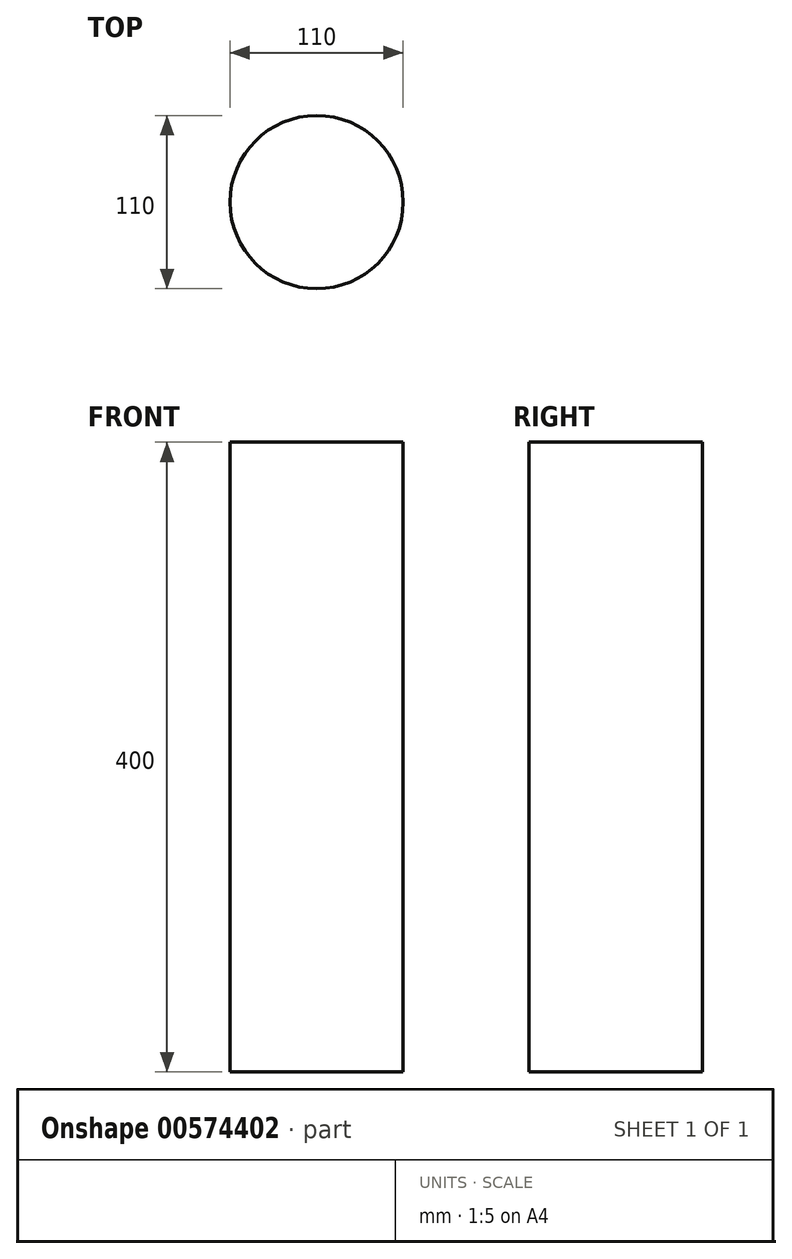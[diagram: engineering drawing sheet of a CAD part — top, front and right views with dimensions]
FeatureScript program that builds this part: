
annotation { "Feature Type Name" : "Feature", "Feature Type Description" : "" }
export const myFeature = defineFeature(function(context is Context, id is Id, definition is map)
    precondition{}
    {
        {
            var Q0;
            Q0=qCreatedBy(makeId("Top.planeOp"),FACE);
            var sketch = newSketch(context, id + "F0", { "sketchPlane" : qUnion([Q0])});
            skCircle(sketch, "E0", {"center": v(0, 0) * mm, "radius": 55 * mm});
            skSolve(sketch);
        }
        {
            var Q0;
            Q0 = qSketchRegion(id + "F0", true);
            extrude(context, id + "F1", {"entities" : qUnion([Q0]), "depth" : 400 * mm, "offsetDistance" : 25 * mm});
        }
    });
